# Revit family: LAMP_MAUI
name_source: partatom
category: Modelos genéricos
revit_build: Autodesk Revit 2015 (Build: 20140606_1530(x64)
units: mm (PartAtom-declared; Revit-internal decimal feet)

## types (8) — shared parameters
CRI = 80
Diameter = 130 mm  [stored 0.426509 ft]
Elevación por defecto = 1219 mm
Fabricante = LAMP
Gear = Electronic
Height = 1150 mm
Initial color = 3000 K
Installation instructions = http://www.lamp.es
Insulation class = II
LED Lifetime = 50.000 L90 B10
Lamp = HIGH POWER LED
Last update = 05/09/2018
Luminaire type = Indoor - Surface downlight
MacAdam = 4
Manufacturer URL = http://www.lamp.es
Manufacturer country = Spain
Manufacturer name = LAMP
Model explanation = Availability of tilting between 0º and 180º when placed in a project.
Power Supply = 220-240V 50-60Hz
Product URL = http://www.lamp.es
Product datasheet = http://www.lamp.es
Protection rating = IP20
Type = HI POWER CREE
Weight = 1.35 kg

## per-type parameters (varying)
| type | Descripción | Efficacy | Finish | IEE | Initial intensity | Material soporte | Modelo | Photometric web file | Plum | Power | Product code |
| 540LM 3000 WHITE 14 BEAM | MAUI SUS 800 WW WH. | 41 lm/W | 9010 Textured | A++ | 540 lm | LAMP_Aluminio cuerpo Maui BL | 7341330 | Cabeza Maui : 540LM 3000 WHITE 14 BEAM | 13 W | 10 W | 7341330 |
| 540LM 3000 YELLOW 14 BEAM | MAUI SUS 800 WW YE. | 41 lm/W | 1021 textured | A++ | 540 lm | LAMP_Aluminio cuerpo Maui AM | 7341331 | Cabeza Maui : 540LM 3000 YELLOW 14 BEAM | 13 W | 10 W | 7341331 |
| 540LM 3000 GRAPHITE 14 BEAM | MAUI SUS 800 WW GRH. | 41 lm/W | Texturised graphite | A++ | 540 lm | LAMP_Aluminio cuerpo Maui GR | 7341332 | Cabeza Maui : 540LM 3000 GRAPHITE 14 BEAM | 13 W | 10 W | 7341332 |
| 540LM 3000 CHROME 14 BEAM | MAUI SUS 800 WW CRM. | 41 lm/W | Gloss grey + Alodine 1500 | A++ | 540 lm | LAMP_Aluminio cuerpo Maui CR | 7341333 | Cabeza Maui : 540LM 3000 CHROME 14 BEAM | 13 W | 10 W | 7341333 |
| 867LM 3000 WHITE 16 BEAM | MAUI SUS 1600 WW WH. | 36 lm/W | 9010 Textured | A+ | 867 lm | LAMP_Aluminio cuerpo Maui BL | 7341340 | Cabeza Maui : 867LM 3000 WHITE 16 BEAM | 24 W | 19 W | 7341340 |
| 867LM 3000 YELLOW 16 BEAM | MAUI SUS 1600 WW YE. | 36 lm/W | 1021 textured | A+ | 867 lm | LAMP_Aluminio cuerpo Maui AM | 7341341 | Cabeza Maui : 867LM 3000 YELLOW 16 BEAM | 24 W | 19 W | 7341341 |
| 867LM 3000 GRAPHITE 16 BEAM | MAUI SUS 1600 WW GRH. | 36 lm/W | Texturised graphite | A+ | 867 lm | LAMP_Aluminio cuerpo Maui GR | 7341342 | Cabeza Maui : 867LM 3000 GRAPHITE 16 BEAM | 24 W | 19 W | 7341342 |
| 867LM 3000 CHROME 16 BEAM | MAUI SUS 1600 WW CRM. | 36 lm/W | Gloss grey + Alodine 1500 | A+ | 867 lm | LAMP_Aluminio cuerpo Maui CR | 7341343 | Cabeza Maui : 867LM 3000 CHROME 16 BEAM | 24 W | 19 W | 7341343 |

note: [stored X ft] marks values corroborated as IEEE doubles in the binary element streams (Revit-internal decimal feet)
